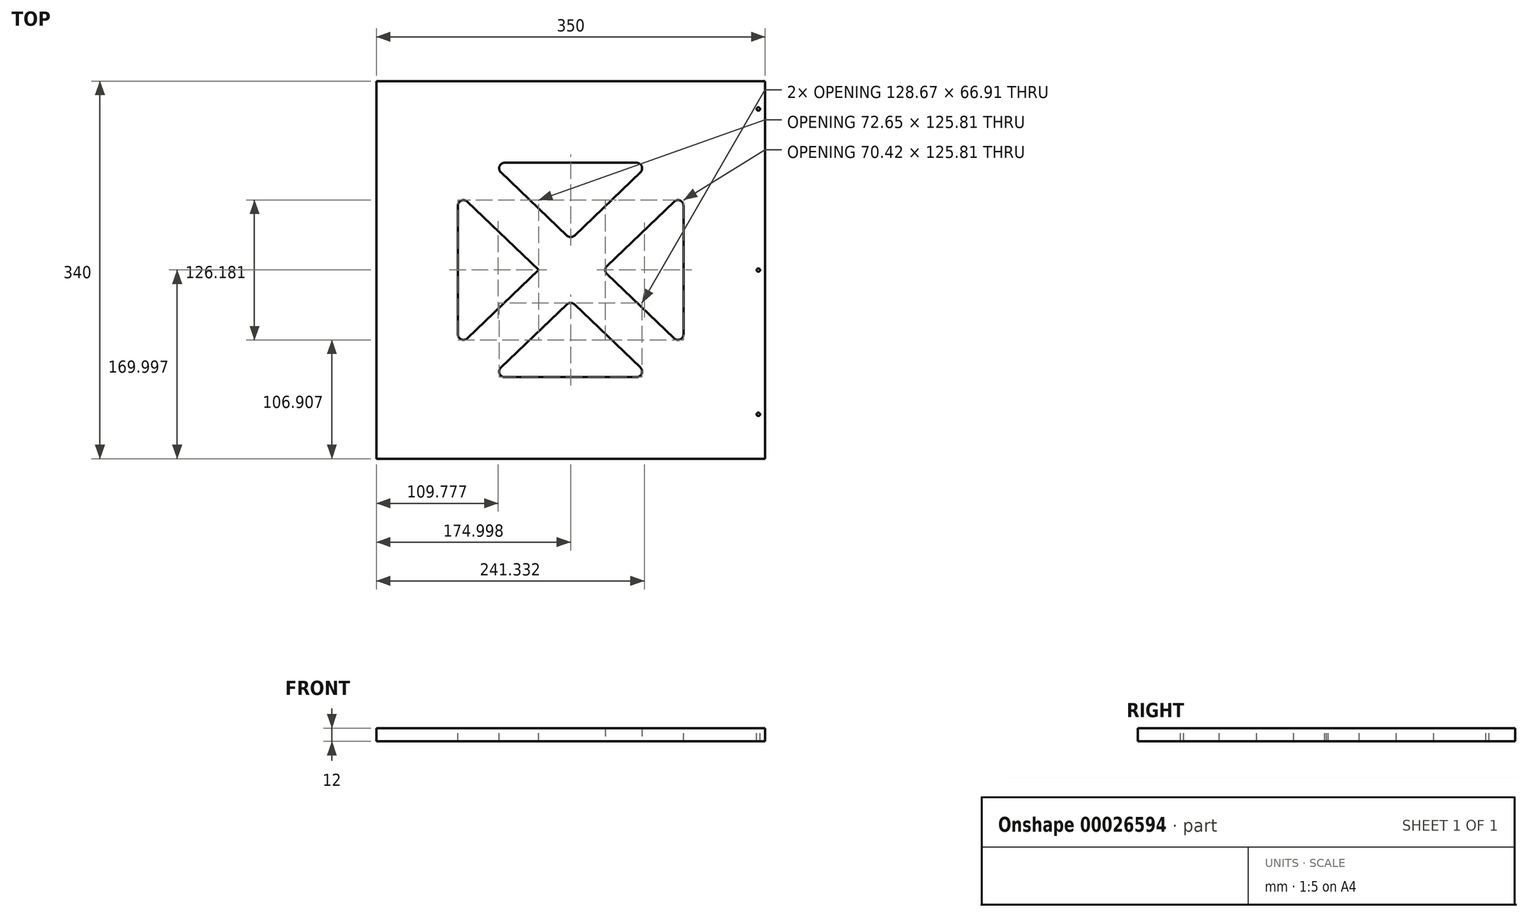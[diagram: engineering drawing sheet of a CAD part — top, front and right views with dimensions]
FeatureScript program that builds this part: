
annotation { "Feature Type Name" : "Feature", "Feature Type Description" : "" }
export const myFeature = defineFeature(function(context is Context, id is Id, definition is map)
    precondition{}
    {
        {
            var Q0;
            Q0=qCreatedBy(makeId("Top.planeOp"),FACE);
            var sketch = newSketch(context, id + "F0", { "sketchPlane" : qUnion([Q0])});
            skLineSegment(sketch, "E0.bottom", {"start": v(-70.96, 65.05) * mm, "end": v(279.04, 65.05) * mm});
            skLineSegment(sketch, "E0.top", {"start": v(-70.96, -274.95) * mm, "end": v(279.04, -274.95) * mm});
            skLineSegment(sketch, "E0.left", {"start": v(-70.96, 65.05) * mm, "end": v(-70.96, -274.95) * mm});
            skLineSegment(sketch, "E0.right", {"start": v(279.04, 65.05) * mm, "end": v(279.04, -274.95) * mm});
            skSolve(sketch);
        }
        {
            var Q0;
            Q0=qSketchRegion(id+"F0",true);
            extrude(context, id + "F1", {"entities" : qUnion([Q0]), "depth" : 12 * mm});
        }
        {
            var Q0;
            Q0=makeQuery(id+"F1.opExtrude","CAP_FACE",FACE,{"disambiguationData":[OSD([sQuery(id+"F0.wireOp",EDGE,"E0.bottom"),sQuery(id+"F0.wireOp",EDGE,"E0.top"),sQuery(id+"F0.wireOp",EDGE,"E0.left"),sQuery(id+"F0.wireOp",EDGE,"E0.right")])],"isStart":false});
            var sketch = newSketch(context, id + "F2", { "sketchPlane" : qUnion([Q0])});
            skLineSegment(sketch, "E1.2", {"start": v(175.83, -8.4) * mm, "end": v(104.04, -77.24) * mm});
            skLineSegment(sketch, "E2.0", {"start": v(205.58, -35.3) * mm, "end": v(132.94, -104.95) * mm});
            skLineSegment(sketch, "E2.1", {"start": v(205.58, -35.3) * mm, "end": v(205.58, -174.61) * mm});
            skLineSegment(sketch, "E2.2", {"start": v(32.25, -201.5) * mm, "end": v(175.83, -201.5) * mm});
            skLineSegment(sketch, "E3.0", {"start": v(2.5, -35.3) * mm, "end": v(75.14, -104.95) * mm});
            skLineSegment(sketch, "E3.1", {"start": v(2.5, -35.3) * mm, "end": v(2.5, -174.61) * mm});
            skLineSegment(sketch, "E4.0", {"start": v(32.25, -8.4) * mm, "end": v(175.83, -8.4) * mm});
            skLineSegment(sketch, "E4.1", {"start": v(32.25, -8.4) * mm, "end": v(104.04, -77.24) * mm});
            skLineSegment(sketch, "E5.trimOffspring", {"start": v(132.94, -104.95) * mm, "end": v(205.58, -174.61) * mm});
            skLineSegment(sketch, "E6.trimOffspring", {"start": v(104.04, -132.66) * mm, "end": v(32.25, -201.5) * mm});
            skLineSegment(sketch, "E7.trimOffspring", {"start": v(104.04, -132.66) * mm, "end": v(175.83, -201.5) * mm});
            skLineSegment(sketch, "E8.trimOffspring", {"start": v(75.14, -104.95) * mm, "end": v(2.5, -174.61) * mm});
            skSolve(sketch);
        }
        {
            var Q0;
            Q0=qSketchRegion(id+"F2",true);
            extrude(context, id + "F3", {"entities" : qUnion([Q0]), "operationType" : NewBodyOperationType.REMOVE, "endBound" : BoundingType.THROUGH_ALL, "oppositeDirection" : true, "depth" : 25 * mm});
        }
        {
            var Q0;
            Q0=makeQuery(id+"F3.boolean.opBoolean","COPY",EDGE,{"derivedFrom":makeQuery(id+"F3.opExtrude","SWEPT_EDGE",EDGE,{"disambiguationData":[OSD([sQuery(id+"F2.wireOp",EDGE,"E3.0"),sQuery(id+"F2.wireOp",EDGE,"E3.1")])]})});
            var Q1;
            Q1=makeQuery(id+"F3.boolean.opBoolean","COPY",EDGE,{"derivedFrom":makeQuery(id+"F3.opExtrude","SWEPT_EDGE",EDGE,{"disambiguationData":[OSD([sQuery(id+"F2.wireOp",EDGE,"E3.1"),sQuery(id+"F2.wireOp",EDGE,"E8.trimOffspring")])]})});
            var Q2;
            Q2=makeQuery(id+"F3.boolean.opBoolean","COPY",EDGE,{"derivedFrom":makeQuery(id+"F3.opExtrude","SWEPT_EDGE",EDGE,{"disambiguationData":[OSD([sQuery(id+"F2.wireOp",EDGE,"E6.trimOffspring"),sQuery(id+"F2.wireOp",EDGE,"E2.2")])]})});
            var Q3;
            Q3=makeQuery(id+"F3.boolean.opBoolean","COPY",EDGE,{"derivedFrom":makeQuery(id+"F3.opExtrude","SWEPT_EDGE",EDGE,{"disambiguationData":[OSD([sQuery(id+"F2.wireOp",EDGE,"E6.trimOffspring"),sQuery(id+"F2.wireOp",EDGE,"E7.trimOffspring")])]})});
            var Q4;
            Q4=makeQuery(id+"F3.boolean.opBoolean","COPY",EDGE,{"derivedFrom":makeQuery(id+"F3.opExtrude","SWEPT_EDGE",EDGE,{"disambiguationData":[OSD([sQuery(id+"F2.wireOp",EDGE,"E7.trimOffspring"),sQuery(id+"F2.wireOp",EDGE,"E2.2")])]})});
            var Q5;
            Q5=makeQuery(id+"F3.boolean.opBoolean","COPY",EDGE,{"derivedFrom":makeQuery(id+"F3.opExtrude","SWEPT_EDGE",EDGE,{"disambiguationData":[OSD([sQuery(id+"F2.wireOp",EDGE,"E2.1"),sQuery(id+"F2.wireOp",EDGE,"E5.trimOffspring")])]})});
            var Q6;
            Q6=makeQuery(id+"F3.boolean.opBoolean","COPY",EDGE,{"derivedFrom":makeQuery(id+"F3.opExtrude","SWEPT_EDGE",EDGE,{"disambiguationData":[OSD([sQuery(id+"F2.wireOp",EDGE,"E2.0"),sQuery(id+"F2.wireOp",EDGE,"E5.trimOffspring")])]})});
            var Q7;
            Q7=makeQuery(id+"F3.boolean.opBoolean","COPY",EDGE,{"derivedFrom":makeQuery(id+"F3.opExtrude","SWEPT_EDGE",EDGE,{"disambiguationData":[OSD([sQuery(id+"F2.wireOp",EDGE,"E2.0"),sQuery(id+"F2.wireOp",EDGE,"E2.1")])]})});
            var Q8;
            Q8=makeQuery(id+"F3.boolean.opBoolean","COPY",EDGE,{"derivedFrom":makeQuery(id+"F3.opExtrude","SWEPT_EDGE",EDGE,{"disambiguationData":[OSD([sQuery(id+"F2.wireOp",EDGE,"E1.2"),sQuery(id+"F2.wireOp",EDGE,"E4.0")])]})});
            var Q9;
            Q9=makeQuery(id+"F3.boolean.opBoolean","COPY",EDGE,{"derivedFrom":makeQuery(id+"F3.opExtrude","SWEPT_EDGE",EDGE,{"disambiguationData":[OSD([sQuery(id+"F2.wireOp",EDGE,"E1.2"),sQuery(id+"F2.wireOp",EDGE,"E4.1")])]})});
            var Q10;
            Q10=makeQuery(id+"F3.boolean.opBoolean","COPY",EDGE,{"derivedFrom":makeQuery(id+"F3.opExtrude","SWEPT_EDGE",EDGE,{"disambiguationData":[OSD([sQuery(id+"F2.wireOp",EDGE,"E4.1"),sQuery(id+"F2.wireOp",EDGE,"E4.0")])]})});
            fillet(context, id + "F4", {"entities" : qUnion([Q0, Q1, Q2, Q3, Q4, Q5, Q6, Q7, Q8, Q9, Q10]), "radius" : 5 * mm, "tangentPropagation" : true, "allowEdgeOverflow" : false});
        }
        {
            var Q0;
            Q0=makeQuery(id+"F1.opExtrude","CAP_FACE",FACE,{"disambiguationData":[OSD([sQuery(id+"F0.wireOp",EDGE,"E0.bottom"),sQuery(id+"F0.wireOp",EDGE,"E0.top"),sQuery(id+"F0.wireOp",EDGE,"E0.left"),sQuery(id+"F0.wireOp",EDGE,"E0.right")])],"isStart":false});
            var sketch = newSketch(context, id + "F5", { "sketchPlane" : qUnion([Q0])});
            skLineSegment(sketch, "E9", {"start": v(-70.96, -104.95) * mm, "end": v(279.04, -108.56) * mm, "construction": true});
            skLineSegment(sketch, "E10", {"start": v(104.04, 65.05) * mm, "end": v(104.04, -274.95) * mm, "construction": true});
            skCircle(sketch, "E11", {"center": v(-64.96, -105.01) * mm, "radius": 1.5 * mm, "construction": true});
            skCircle(sketch, "E12", {"center": v(-64.96, 40.05) * mm, "radius": 1.5 * mm, "construction": true});
            skCircle(sketch, "E13", {"center": v(-64.96, -234.95) * mm, "radius": 1.5 * mm, "construction": true});
            skCircle(sketch, "E14.MirrorC", {"center": v(273.04, 40.05) * mm, "radius": 1.5 * mm});
            skCircle(sketch, "E15.MirrorC", {"center": v(273.04, -234.95) * mm, "radius": 1.5 * mm});
            skCircle(sketch, "E16.MirrorC", {"center": v(273.04, -105.01) * mm, "radius": 1.5 * mm});
            skSolve(sketch);
        }
        {
            var Q0;
            Q0=qSketchRegion(id+"F5",true);
            extrude(context, id + "F6", {"entities" : qUnion([Q0]), "operationType" : NewBodyOperationType.REMOVE, "endBound" : BoundingType.THROUGH_ALL, "oppositeDirection" : true, "depth" : 25 * mm});
        }
    });
